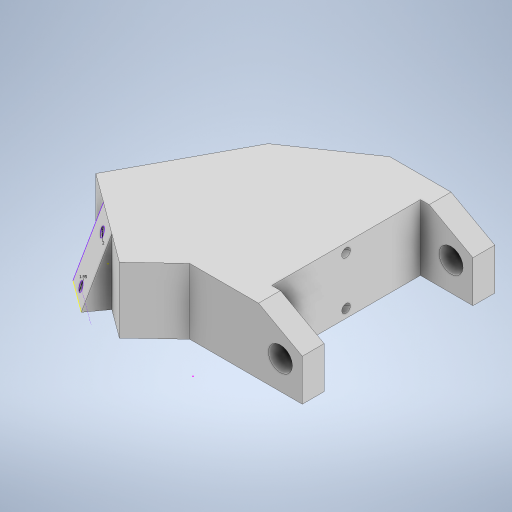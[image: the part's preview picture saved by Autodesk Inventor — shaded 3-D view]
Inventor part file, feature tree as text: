
AUTODESK INVENTOR PART (.ipt)
format: ipt  version: 2024 (Build 280153000, 153)  size: 808,960 bytes
history: native  units: mm
features: sketch x58, extrude x44, move_body x9, plane x6, split x6, boolean_combine x4, chamfer x3, loft x2, delete_face x1
ambient origin geometry x8: Origin, YZ Plane, XZ Plane, XY Plane, X Axis, Y Axis, Z Axis, Center Point
bodies: Solid1 (feature_tree), Solid2 (feature_tree), Solid3 (feature_tree), Solid4 (feature_tree), Solid5 (feature_tree), Solid6 (feature_tree), Solid7 (feature_tree), Solid8 (feature_tree), Solid9 (feature_tree), Solid10 (feature_tree), Solid11 (feature_tree), Solid12 (feature_tree), Solid13 (feature_tree)
feature tree (133):
  extrude  "Extrusion1"  Depth=16.0mm
  sketch  "Sketch2"  dims[d2=15.0mm d3=0.0mm d4=10.0mm]
  extrude  "Extrusion2"  Depth=10.0mm
  chamfer  "Chamfer1"  Distance=21.25mm
  extrude  "Extrusion3"  Depth=10.0mm TaperAngle=0.0deg
  extrude  "Extrusion4"  Depth=11.5mm TaperAngle=0.0deg
  extrude  "Extrusion5"  Depth=1.0mm TaperAngle=0.0deg
  chamfer  "Chamfer2"  Distance=6.0mm Angle=45.0deg
  sketch  "Sketch6"  dims[d14=7.0mm d15=11.5mm d16=0.0mm]
  extrude  "Extrusion6"  Depth=9.0mm
  extrude  "Extrusion7"  Depth=45.25mm TaperAngle=0.0deg
  chamfer  "Chamfer3"  Distance=11.5mm Angle=45.0deg
  sketch  "Sketch9"  dims[d26=3.3mm d27=45.25mm d28=0.0mm d29=11.5mm d30=5.5mm d31=45.0deg]
  extrude  "Extrusion8"  Depth=65.75mm TaperAngle=0.0deg
  extrude  "Extrusion9"  Depth=9.0mm TaperAngle=0.0deg
  extrude  "Extrusion10"  Depth=13.0mm TaperAngle=0.0deg
  sketch  "Sketch13"  dims[d43=24.0mm d44=21.0mm d45=0.0mm]
  extrude  "Extrusion11"  Depth=21.0mm TaperAngle=0.0deg
  extrude  "Extrusion12"  TaperAngle=0.0deg  [1 undecoded]
  extrude  "Extrusion13"  Depth=1.0mm
  plane  "Work Plane1"
  split  "Split1"
  move_body  "Move Body1"
  extrude  "Extrusion14"  Depth=1.5mm TaperAngle=0.0deg
  delete_face  "Delete Face1"
  extrude  "Extrusion17"  Depth=1.0mm
  extrude  "Extrusion18"  Depth=1.2mm TaperAngle=0.0deg
  extrude  "Extrusion19"  [1 undecoded]
  extrude  "Extrusion20"  Depth=1.75mm
  plane  "Work Plane2"
  split  "Split2"
  move_body  "Move Body2"
  boolean_combine  "Combine1"
  plane  "Work Plane3"
  split  "Split3"
  move_body  "Move Body3"
  boolean_combine  "Combine2"
  split  "Split4"
  split  "Split5"
  move_body  "Move Body4"
  move_body  "Move Body5"
  extrude  "Extrusion22"  Depth=20.0mm TaperAngle=0.0deg
  extrude  "Extrusion23"  Depth=12.0mm
  move_body  "Move Body6"
  move_body  "Move Body7"
  boolean_combine  "Combine3"
  extrude  "Extrusion24"  Depth=12.0mm TaperAngle=0.0deg
  plane  "Work Plane5"
  sketch  "Sketch32"  dims[d110=8.0mm d111=0.0mm d112=5.5mm]
  plane  "Work Plane6"
  extrude  "Extrusion27"  Depth=8.0mm TaperAngle=0.0deg
  plane  "Work Plane4"
  extrude  "Extrusion28"  Depth=123.0mm TaperAngle=0.0deg
  sketch  "Sketch35"  dims[d121=2.0mm d122=0.0mm d123=8.0mm d124=0.0mm]
  extrude  "Extrusion29"  Depth=82.0mm TaperAngle=0.0deg
  extrude  "Extrusion30"  Depth=5.5mm
  extrude  "Extrusion31"  Depth=40.0mm TaperAngle=0.0deg
  sketch  "Sketch38"  dims[d131=15.0mm d132=0.0mm d133=15.0mm d134=0.0mm]
  extrude  "Extrusion32"  Depth=2.0mm TaperAngle=0.0deg
  extrude  "Extrusion33"  Depth=8.0mm TaperAngle=0.0deg
  extrude  "Extrusion34"  Depth=25.394541mm
  extrude  "Extrusion35"  Depth=15.0mm TaperAngle=0.0deg
  extrude  "Extrusion36"  Depth=15.0mm TaperAngle=0.0deg
  extrude  "Extrusion37"  Depth=15.0mm TaperAngle=0.0deg
  extrude  "Extrusion38"  Depth=15.0mm TaperAngle=0.0deg
  extrude  "Extrusion39"  Depth=6.75mm TaperAngle=0.0deg
  extrude  "Extrusion40"  Depth=10.0mm
  extrude  "Extrusion41"  Depth=2.0mm TaperAngle=0.0deg
  extrude  "Extrusion42"  Depth=9.0mm
  extrude  "Extrusion43"  Depth=20.5mm TaperAngle=0.0deg
  extrude  "Extrusion44"  Depth=20.5mm TaperAngle=0.0deg
  split  "Split6"
  move_body  "Move Body8"
  extrude  "Extrusion45"  TaperAngle=0.0deg  [1 undecoded]
  move_body  "Move Body9"
  boolean_combine  "Combine4"
  extrude  "Extrusion46"  Depth=22.0mm TaperAngle=0.0deg
  extrude  "Extrusion47"  Depth=1.95mm
  sketch  "Sketch56"
  sketch  "Sketch57"
  extrude  "Extrusion48"  TaperAngle=0.0deg  [1 undecoded]
  loft  "Loft1"
  extrude  "Extrusion49"  Depth=0.872665mm
  loft  "Loft2"
  sketch  "Sketch62"
  sketch  "Sketch63"
  sketch  "Sketch1"  dims[d0=36.0mm d1=16.0mm]
  sketch  "Sketch3"  dims[d5=10.0mm]
  sketch  "Sketch4"  dims[d6=3.3mm d7=21.25mm d8=0.0mm]
  sketch  "Sketch5"  dims[d9=10.0mm d10=5.5mm d11=45.0deg d12=10.0mm d13=0.0mm]
  sketch  "Sketch7"  dims[d17=3.3mm d18=1.0mm d19=0.0mm d20=6.0mm d21=11.5mm d22=45.0deg]
  sketch  "Sketch8"  dims[d23=15.0mm d24=0.0mm d25=9.0mm]
  sketch  "Sketch10"  dims[d32=2.0mm d33=65.75mm d34=0.0mm]
  sketch  "Sketch11"  dims[d35=0.5mm d36=0.0mm d37=9.0mm d38=0.0mm]
  sketch  "Sketch12"  dims[d39=0.5mm d40=0.0mm d41=13.0mm d42=0.0mm]
  sketch  "Sketch14"  dims[d46=12.25mm d47=-12.0mm d48=0.0mm d49=0.0mm]
  sketch  "Sketch15"  dims[d50=10.0mm d51=0.0mm d61=1.0mm]
  sketch  "Sketch16"  dims[d62=1.0mm d63=1.5mm d64=0.0mm]
  sketch  "Sketch17"  dims[d65=1.0mm d66=1.0mm]
  sketch  "Sketch20"  dims[d67=5.5mm d68=0.0mm d69=1.2mm d70=0.0mm]
  sketch  "Sketch21"  dims[d71=2.2mm d72=0.0mm d73=-5.5mm]
  sketch  "Sketch22"  dims[d74=-3.0mm d75=0.0mm d76=0.0mm d79=1.75mm]
  sketch  "Sketch23"  dims[d80=3.0mm d81=0.0mm d82=0.0mm d83=0.0mm d84=0.0mm d85=20.0mm]
  sketch  "Sketch25"  dims[d86=0.0mm d87=0.0mm d88=-20.0mm d89=12.0mm]
  sketch  "Sketch26"  dims[d90=12.0mm d91=0.0mm d92=12.0mm d93=0.0mm]
  sketch  "Sketch27"  dims[d94=0.0mm d95=0.0mm d96=-8.0mm d97=0.0mm d98=0.0mm d99=8.0mm]
  sketch  "Sketch28"  dims[d100=4.5mm d101=123.0mm d102=0.0mm]
  sketch  "Sketch29"  dims[d107=5.1mm d108=82.0mm d109=0.0mm]
  sketch  "Sketch33"  dims[d113=40.0mm d114=0.0mm d115=40.0mm d116=0.0mm]
  sketch  "Sketch34"  dims[d117=40.0mm d118=0.0mm d119=2.0mm d120=0.0mm]
  sketch  "Sketch36"  dims[d125=20.0mm d126=25.394541mm]
  sketch  "Sketch37"  dims[d127=15.0mm d128=0.0mm d129=15.0mm d130=0.0mm]
  sketch  "Sketch39"  dims[d135=15.0mm d136=0.0mm d137=15.0mm d138=0.0mm]
  sketch  "Sketch40"  dims[d139=6.3338mm d140=15.0mm d141=0.0mm]
  sketch  "Sketch41"  dims[d142=15.0mm d143=0.0mm d144=6.75mm d145=0.0mm]
  sketch  "Sketch42"  dims[d146=30.0mm d147=0.0mm d148=10.0mm]
  sketch  "Sketch43"  dims[d149=-5.0mm d150=0.0mm d151=0.0mm d152=2.0mm d153=0.0mm]
  sketch  "Sketch44"  dims[d154=3.0mm d155=0.0mm d156=0.0mm d157=9.0mm]
  sketch  "Sketch45"  dims[d158=5.0mm d159=0.0mm d160=20.5mm d161=0.0mm]
  sketch  "Sketch46"  dims[d165=1.95mm d166=20.5mm d167=0.0mm]
  sketch  "Sketch47"  dims[d169=2.0mm d170=0.0mm d171=90.0deg]
  sketch  "Sketch48"  dims[d172=0.0mm d173=90.0deg d174=22.0mm d175=0.0mm]
  sketch  "Sketch49"  dims[d177=1.95mm d179=1.95mm]
  sketch  "Sketch50"  dims[d180=0.0mm d181=90.0deg d182=0.0mm d183=90.0deg]
  sketch  "Sketch51"  dims[d185=1.95mm d188=2.0mm]
  sketch  "Sketch52"  dims[d52=0.5mm d53=0.872665mm]
  sketch  "Sketch53"  dims[d103=0.5mm d104=0.872665mm]
  sketch  "Sketch54"
  sketch  "Sketch55"
  sketch  "Sketch58"
  sketch  "Sketch59"
  sketch  "Sketch60"
  sketch  "Sketch61"
note: 4 required parameter values undecoded (feature->parameter linkage not recoverable at this tier; creation-order binding heuristic only, values carry confidence <= 0.55)
